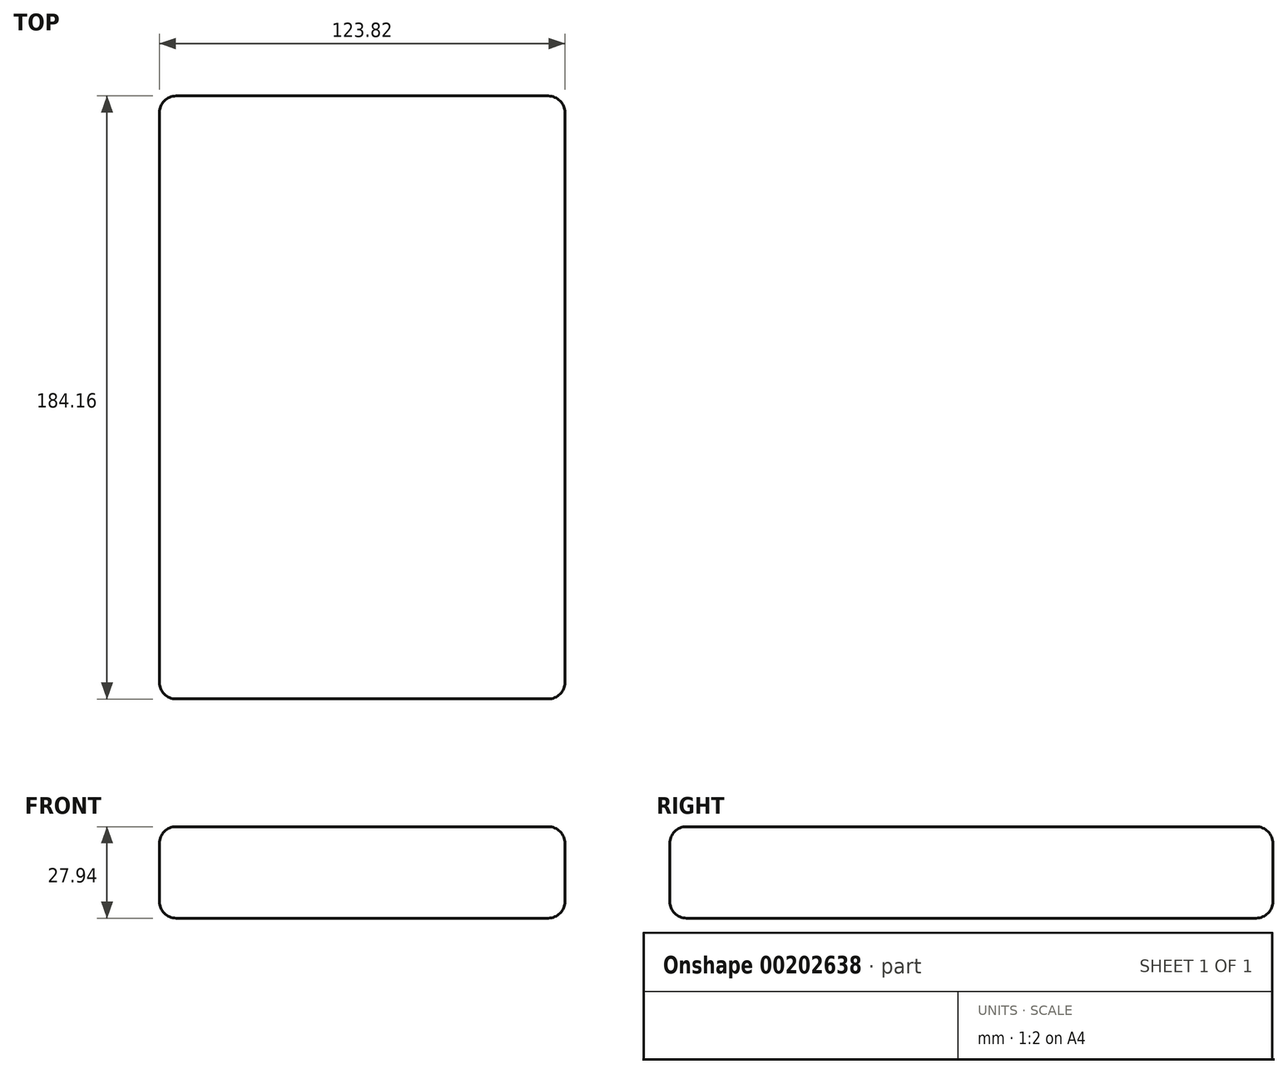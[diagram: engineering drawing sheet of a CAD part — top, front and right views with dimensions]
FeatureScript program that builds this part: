
annotation { "Feature Type Name" : "Feature", "Feature Type Description" : "" }
export const myFeature = defineFeature(function(context is Context, id is Id, definition is map)
    precondition{}
    {
        {
            var Q0;
            Q0=qCreatedBy(makeId("Top.planeOp"),FACE);
            var sketch = newSketch(context, id + "F0", { "sketchPlane" : qUnion([Q0])});
            skLineSegment(sketch, "E0.bottom", {"start": v(-61.91, 92.07) * mm, "end": v(61.91, 92.07) * mm});
            skLineSegment(sketch, "E0.top", {"start": v(-61.91, -92.08) * mm, "end": v(61.91, -92.08) * mm});
            skLineSegment(sketch, "E0.left", {"start": v(-61.91, 92.07) * mm, "end": v(-61.91, -92.08) * mm});
            skLineSegment(sketch, "E0.right", {"start": v(61.91, 92.08) * mm, "end": v(61.91, -92.08) * mm});
            skPoint(sketch, "E0.middle", {"position": v(0, 0) * mm});
            skSolve(sketch);
        }
        {
            var Q0;
            Q0=makeQuery(id+"F0.imprint","IMPRINT",FACE,{"disambiguationData":[TD([[makeQuery(id+"F0.imprint","IMPRINT",EDGE,{"derivedFrom":sQuery(id+"F0.wireOp",EDGE,"E0.bottom")}),-1.0]])]});
            extrude(context, id + "F1", {"entities" : qUnion([Q0]), "endBound" : BoundingType.SYMMETRIC, "depth" : 27.94 * mm});
        }
        {
            var Q0;
            Q0=makeQuery(id+"F1.opExtrude","SWEPT_EDGE",EDGE,{"disambiguationData":[OSD([sQuery(id+"F0.wireOp",EDGE,"E0.top"),sQuery(id+"F0.wireOp",EDGE,"E0.left")])]});
            var Q1;
            Q1=makeQuery(id+"F1.opExtrude","SWEPT_EDGE",EDGE,{"disambiguationData":[OSD([sQuery(id+"F0.wireOp",EDGE,"E0.top"),sQuery(id+"F0.wireOp",EDGE,"E0.right")])]});
            var Q2;
            Q2=makeQuery(id+"F1.opExtrude","SWEPT_EDGE",EDGE,{"disambiguationData":[OSD([sQuery(id+"F0.wireOp",EDGE,"E0.bottom"),sQuery(id+"F0.wireOp",EDGE,"E0.right")])]});
            var Q3;
            Q3=makeQuery(id+"F1.opExtrude","SWEPT_EDGE",EDGE,{"disambiguationData":[OSD([sQuery(id+"F0.wireOp",EDGE,"E0.bottom"),sQuery(id+"F0.wireOp",EDGE,"E0.left")])]});
            fillet(context, id + "F2", {"entities" : qUnion([Q0, Q1, Q2, Q3]), "radius" : 5.08 * mm, "tangentPropagation" : true, "allowEdgeOverflow" : false});
        }
        {
            var Q0;
            Q0=makeQuery(id+"F1.opExtrude","CAP_EDGE",EDGE,{"disambiguationData":[OSD([sQuery(id+"F0.wireOp",EDGE,"E0.right")])],"isStart":false});
            var Q1;
            Q1=makeQuery(id+"F1.opExtrude","CAP_EDGE",EDGE,{"disambiguationData":[OSD([sQuery(id+"F0.wireOp",EDGE,"E0.right")])],"isStart":true});
            fillet(context, id + "F3", {"entities" : qUnion([Q0, Q1]), "radius" : 5.08 * mm, "tangentPropagation" : true, "allowEdgeOverflow" : false});
        }
    });
